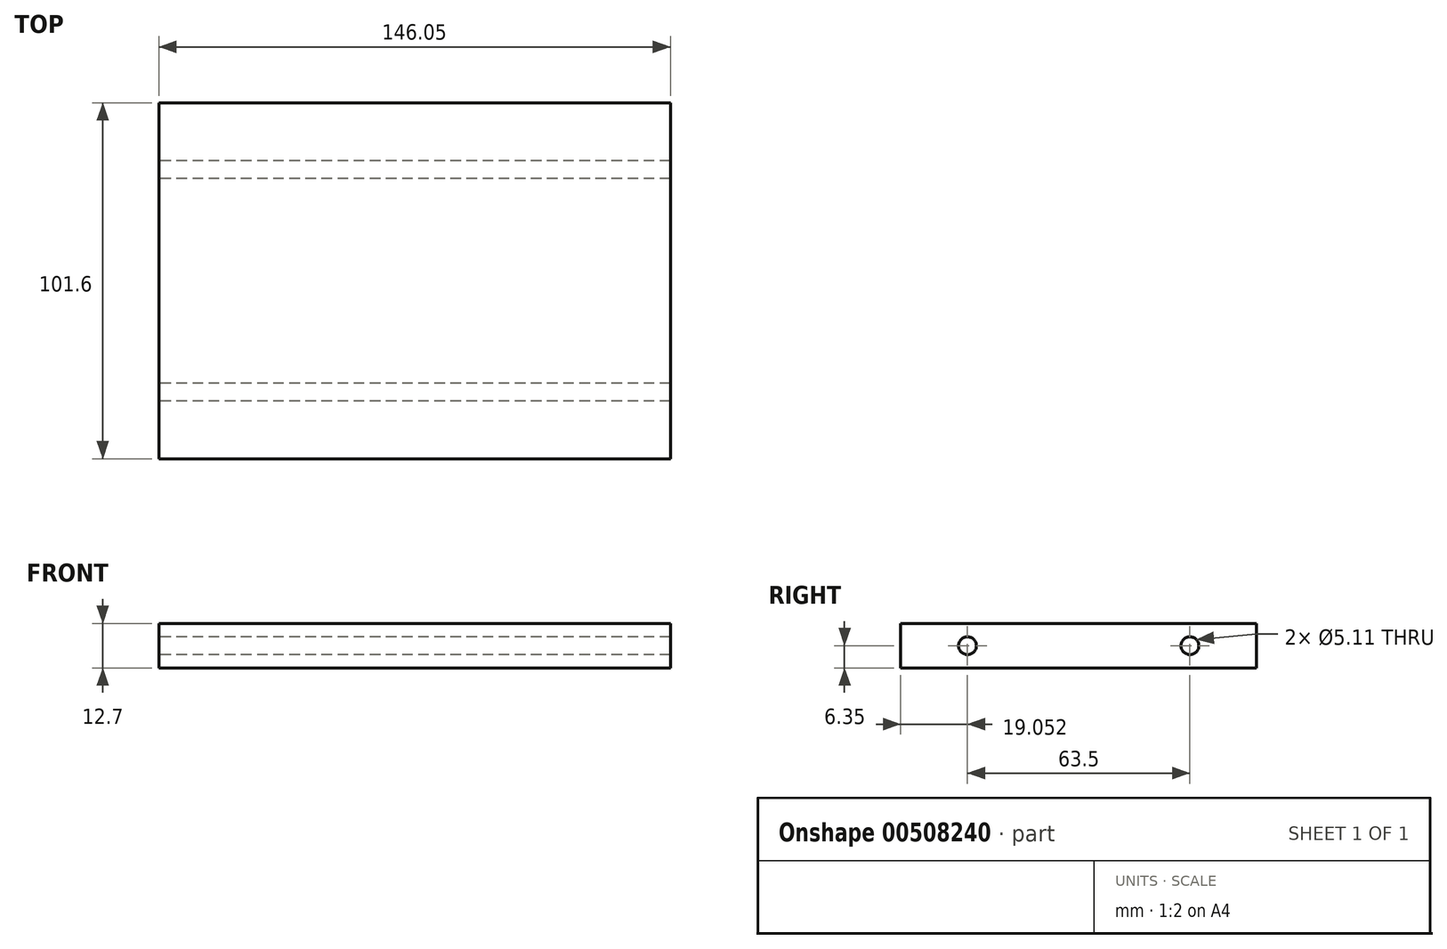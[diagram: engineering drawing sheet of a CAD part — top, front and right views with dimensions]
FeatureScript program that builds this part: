
annotation { "Feature Type Name" : "Feature", "Feature Type Description" : "" }
export const myFeature = defineFeature(function(context is Context, id is Id, definition is map)
    precondition{}
    {
        {
            var Q0;
            Q0=qCreatedBy(makeId("Top.planeOp"),FACE);
            var sketch = newSketch(context, id + "F0", { "sketchPlane" : qUnion([Q0])});
            skLineSegment(sketch, "E0.bottom", {"start": v(-78.98, 53.6) * mm, "end": v(67.07, 53.6) * mm});
            skLineSegment(sketch, "E0.top", {"start": v(-78.98, -48) * mm, "end": v(67.07, -48) * mm});
            skLineSegment(sketch, "E0.left", {"start": v(-78.98, 53.6) * mm, "end": v(-78.98, -48) * mm});
            skLineSegment(sketch, "E0.right", {"start": v(67.07, 53.6) * mm, "end": v(67.07, -48) * mm});
            skSolve(sketch);
        }
        {
            var Q0;
            Q0=makeQuery(id+"F0.imprint","IMPRINT",FACE,{"disambiguationData":[TD([[makeQuery(id+"F0.imprint","IMPRINT",EDGE,{"derivedFrom":sQuery(id+"F0.wireOp",EDGE,"E0.bottom")}),-1.0]])]});
            extrude(context, id + "F1", {"entities" : qUnion([Q0]), "depth" : 12.7 * mm});
        }
        {
            var Q0;
            Q0=makeQuery(id+"F1.opExtrude","SWEPT_FACE",FACE,{"disambiguationData":[OSD([sQuery(id+"F0.wireOp",EDGE,"E0.left")])]});
            var sketch = newSketch(context, id + "F2", { "sketchPlane" : qUnion([Q0])});
            skPoint(sketch, "E1", {"position": v(-34.54, 6.35) * mm});
            skPoint(sketch, "E2", {"position": v(28.96, 6.35) * mm});
            skSolve(sketch);
        }
        {
            var Q0;
            Q0=sQuery(id+"F2.wireOp",VERTEX,"E1");
            var Q1;
            Q1=sQuery(id+"F2.wireOp",VERTEX,"E2");
            var Q2;
            Q2=makeQuery(id+"F1.opExtrude","SWEPT_BODY",BODY,{"disambiguationData":[OSD([sQuery(id+"F0.wireOp",EDGE,"E0.bottom"),sQuery(id+"F0.wireOp",EDGE,"E0.top"),sQuery(id+"F0.wireOp",EDGE,"E0.left"),sQuery(id+"F0.wireOp",EDGE,"E0.right")])]});
            hole(context, id + "F3", {"style" : HoleStyle.SIMPLE, "endStyle" : HoleEndStyle.THROUGH, "standardTappedOrClearance" : lookupTablePath({ "standard" : "ANSI", "engagement" : "75%", "pitch" : "20 tpi", "size" : "1/4", "type" : "Tapped" }), "standardBlindInLast" : lookupTablePath({ "standard" : "ANSI", "engagement" : "75%", "pitch" : "20 tpi", "size" : "1/4", "type" : "Tapped" }), "holeDiameter" : 5.1 * mm, "showTappedDepth" : true, "tappedDepth" : 19.05 * mm, "tapClearance" : 3, "startFromSketch" : true, "locations" : qUnion([Q0, Q1]), "scope" : qUnion([Q2]), "majorDiameter" : 6.35 * mm});
        }
    });
